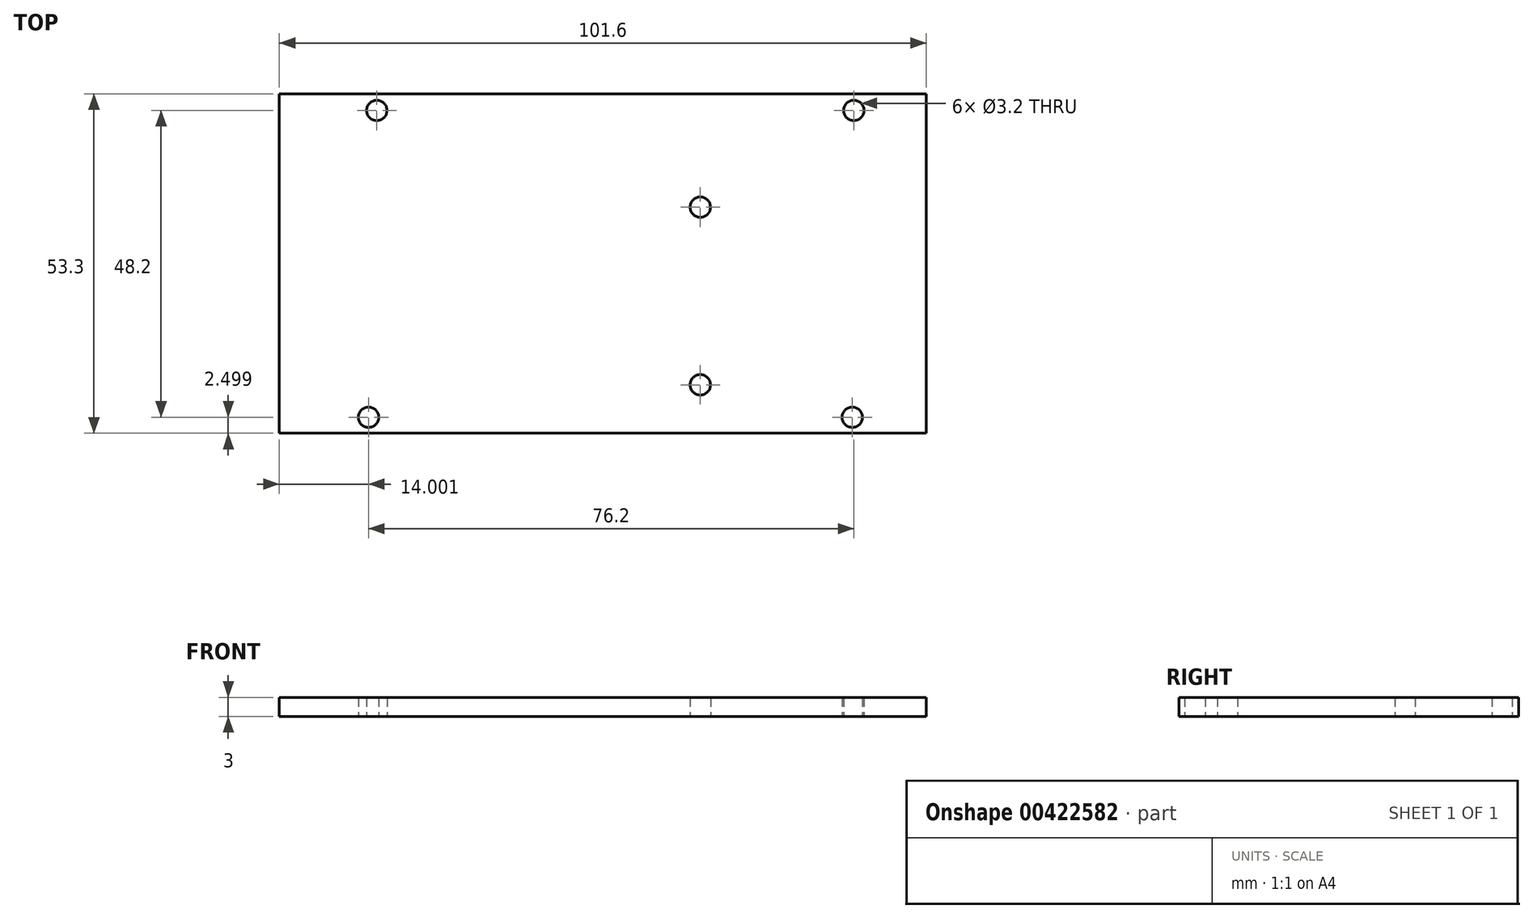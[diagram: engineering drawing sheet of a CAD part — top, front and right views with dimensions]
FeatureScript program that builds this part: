
annotation { "Feature Type Name" : "Feature", "Feature Type Description" : "" }
export const myFeature = defineFeature(function(context is Context, id is Id, definition is map)
    precondition{}
    {
        {
            var Q0;
            Q0=qCreatedBy(makeId("Top.planeOp"),FACE);
            var sketch = newSketch(context, id + "F0", { "sketchPlane" : qUnion([Q0])});
            skLineSegment(sketch, "E0", {"start": v(-45.7, 29.3) * mm, "end": v(-45.7, -24) * mm});
            skLineSegment(sketch, "E1", {"start": v(-45.7, -24) * mm, "end": v(55.9, -24) * mm});
            skLineSegment(sketch, "E2", {"start": v(55.9, -24) * mm, "end": v(55.9, 29.3) * mm});
            skCircle(sketch, "E3", {"center": v(-31.7, -21.5) * mm, "radius": 1.6 * mm});
            skCircle(sketch, "E4", {"center": v(44.5, 26.7) * mm, "radius": 1.6 * mm});
            skLineSegment(sketch, "E5", {"start": v(-31.7, -21.5) * mm, "end": v(-31.7, -24) * mm, "construction": true});
            skCircle(sketch, "E6", {"center": v(-30.4, 26.7) * mm, "radius": 1.6 * mm});
            skLineSegment(sketch, "E7", {"start": v(-30.4, 26.7) * mm, "end": v(-31.7, 26.7) * mm, "construction": true});
            skLineSegment(sketch, "E8", {"start": v(-31.7, 26.7) * mm, "end": v(-31.7, -21.5) * mm, "construction": true});
            skLineSegment(sketch, "E9", {"start": v(-31.7, 26.7) * mm, "end": v(-45.7, 26.7) * mm, "construction": true});
            skLineSegment(sketch, "E10", {"start": v(-30.4, 26.7) * mm, "end": v(20.4, 26.7) * mm, "construction": true});
            skLineSegment(sketch, "E11", {"start": v(20.4, 26.7) * mm, "end": v(20.4, 11.5) * mm, "construction": true});
            skCircle(sketch, "E12", {"center": v(20.4, 11.5) * mm, "radius": 1.6 * mm});
            skCircle(sketch, "E13", {"center": v(20.4, -16.4) * mm, "radius": 1.6 * mm});
            skLineSegment(sketch, "E14", {"start": v(20.4, 11.5) * mm, "end": v(20.4, -16.4) * mm, "construction": true});
            skLineSegment(sketch, "E15", {"start": v(20.4, 26.7) * mm, "end": v(44.5, 26.7) * mm, "construction": true});
            skCircle(sketch, "E16", {"center": v(44.26, -21.5) * mm, "radius": 1.6 * mm});
            skLineSegment(sketch, "E17", {"start": v(-45.7, 29.3) * mm, "end": v(55.9, 29.3) * mm});
            skSolve(sketch);
        }
        {
            var Q0;
            Q0=makeQuery(id+"F0.imprint","IMPRINT",FACE,{"disambiguationData":[TD([[makeQuery(id+"F0.imprint","IMPRINT",EDGE,{"derivedFrom":sQuery(id+"F0.wireOp",EDGE,"E0")}),1.0]])]});
            extrude(context, id + "F1", {"entities" : qUnion([Q0]), "depth" : 3 * mm});
        }
    });
